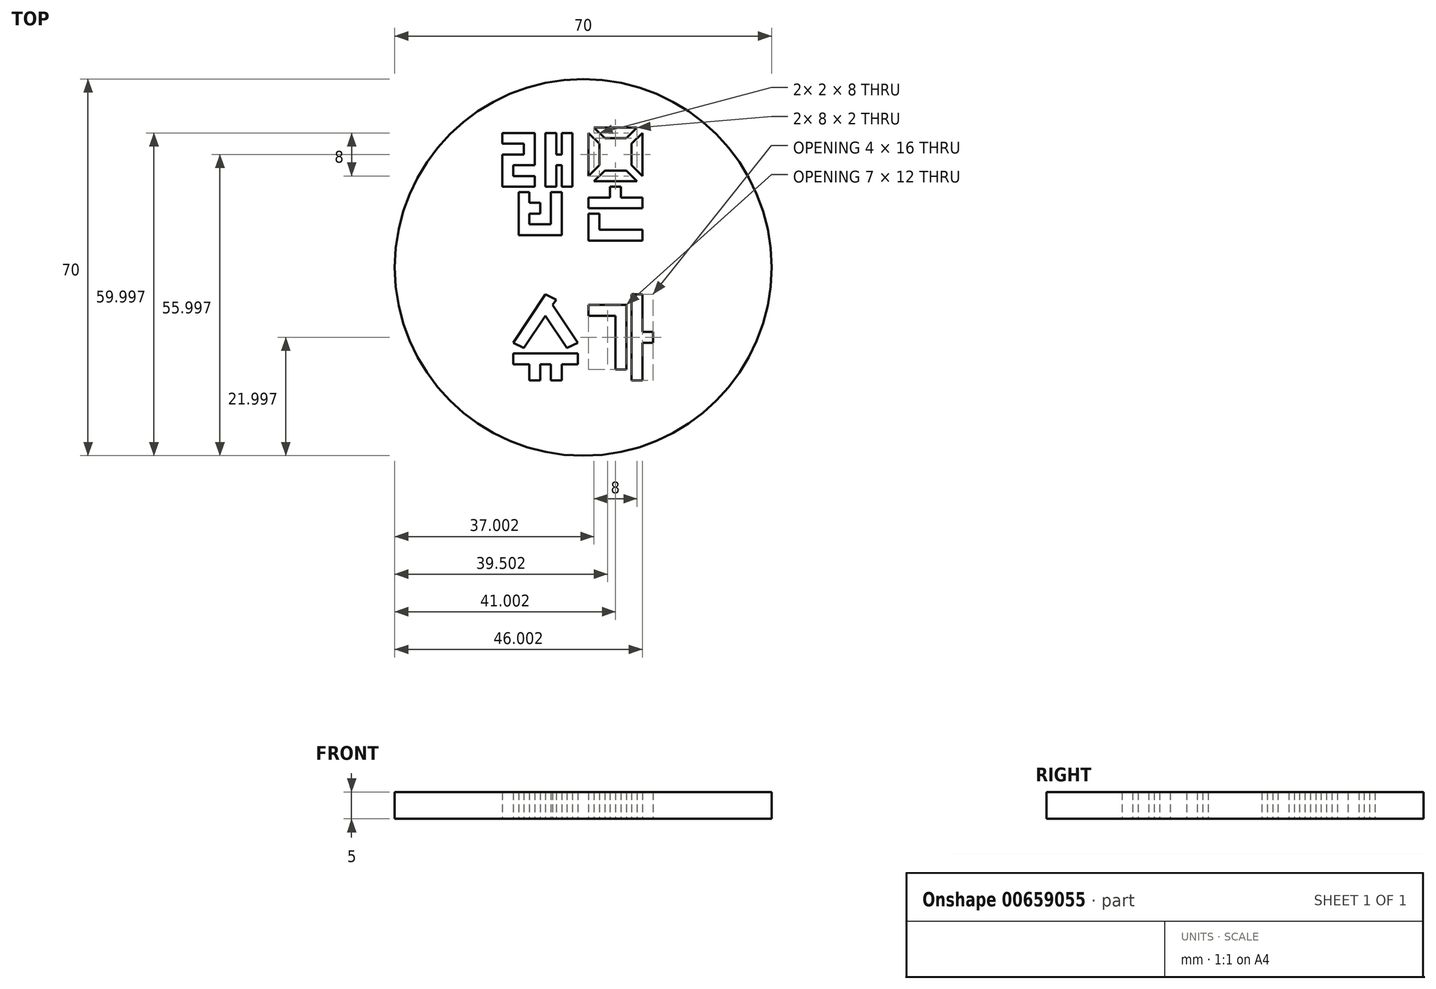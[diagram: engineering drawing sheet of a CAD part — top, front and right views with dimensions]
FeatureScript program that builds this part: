
annotation { "Feature Type Name" : "Feature", "Feature Type Description" : "" }
export const myFeature = defineFeature(function(context is Context, id is Id, definition is map)
    precondition{}
    {
        {
            var Q0;
            Q0=qCreatedBy(makeId("Top.planeOp"),FACE);
            var sketch = newSketch(context, id + "F0", { "sketchPlane" : qUnion([Q0])});
            skLineSegment(sketch, "E0.bottom", {"start": v(-66.05, 21.55) * mm, "end": v(-56.05, 21.55) * mm});
            skLineSegment(sketch, "E0.top", {"start": v(-66.05, 11.55) * mm, "end": v(-60.05, 11.55) * mm});
            skLineSegment(sketch, "E0.left", {"start": v(-66.05, 21.55) * mm, "end": v(-66.05, 19.55) * mm});
            skLineSegment(sketch, "E0.right", {"start": v(-53.05, 21.55) * mm, "end": v(-53.05, 11.55) * mm});
            skLineSegment(sketch, "E1", {"start": v(-66.05, 21.55) * mm, "end": v(-60.05, 21.55) * mm});
            skLineSegment(sketch, "E2", {"start": v(-58.05, 21.55) * mm, "end": v(-58.05, 11.55) * mm});
            skLineSegment(sketch, "E3", {"start": v(-58.05, 11.55) * mm, "end": v(-56.05, 11.55) * mm});
            skLineSegment(sketch, "E4", {"start": v(-56.05, 11.55) * mm, "end": v(-56.05, 15.55) * mm});
            skLineSegment(sketch, "E5", {"start": v(-56.05, 15.55) * mm, "end": v(-55.05, 15.55) * mm});
            skLineSegment(sketch, "E6", {"start": v(-55.05, 15.55) * mm, "end": v(-55.05, 11.55) * mm});
            skLineSegment(sketch, "E7", {"start": v(-56.05, 21.55) * mm, "end": v(-56.05, 17.55) * mm});
            skLineSegment(sketch, "E8", {"start": v(-56.05, 17.55) * mm, "end": v(-55.05, 17.55) * mm});
            skLineSegment(sketch, "E9", {"start": v(-55.05, 17.55) * mm, "end": v(-55.05, 21.55) * mm});
            skLineSegment(sketch, "E10", {"start": v(-60.05, 21.55) * mm, "end": v(-60.05, 15.55) * mm});
            skLineSegment(sketch, "E11", {"start": v(-60.05, 15.55) * mm, "end": v(-64.05, 15.55) * mm});
            skLineSegment(sketch, "E12", {"start": v(-64.05, 15.55) * mm, "end": v(-64.05, 13.55) * mm});
            skLineSegment(sketch, "E13", {"start": v(-64.05, 13.55) * mm, "end": v(-60.05, 13.55) * mm});
            skLineSegment(sketch, "E14", {"start": v(-60.05, 13.55) * mm, "end": v(-60.05, 11.55) * mm});
            skLineSegment(sketch, "E15", {"start": v(-66.05, 19.55) * mm, "end": v(-62.05, 19.55) * mm});
            skLineSegment(sketch, "E16", {"start": v(-62.05, 19.55) * mm, "end": v(-62.05, 17.55) * mm});
            skLineSegment(sketch, "E17", {"start": v(-62.05, 17.55) * mm, "end": v(-66.05, 17.55) * mm});
            skLineSegment(sketch, "E18", {"start": v(-55.05, 10.55) * mm, "end": v(-55.05, 2.55) * mm});
            skLineSegment(sketch, "E19", {"start": v(-55.05, 2.55) * mm, "end": v(-63.05, 2.55) * mm});
            skLineSegment(sketch, "E20", {"start": v(-63.05, 2.55) * mm, "end": v(-63.05, 10.55) * mm});
            skLineSegment(sketch, "E21", {"start": v(-63.05, 10.55) * mm, "end": v(-61.05, 10.55) * mm});
            skLineSegment(sketch, "E22", {"start": v(-61.05, 10.55) * mm, "end": v(-61.05, 8.55) * mm});
            skLineSegment(sketch, "E23", {"start": v(-61.05, 8.55) * mm, "end": v(-59.05, 8.55) * mm});
            skLineSegment(sketch, "E24", {"start": v(-59.05, 8.55) * mm, "end": v(-59.05, 6.55) * mm});
            skLineSegment(sketch, "E25", {"start": v(-59.05, 6.55) * mm, "end": v(-61.05, 6.55) * mm});
            skLineSegment(sketch, "E26", {"start": v(-61.05, 6.55) * mm, "end": v(-61.05, 4.55) * mm});
            skLineSegment(sketch, "E27", {"start": v(-61.05, 4.55) * mm, "end": v(-57.05, 4.55) * mm});
            skLineSegment(sketch, "E28", {"start": v(-57.05, 4.55) * mm, "end": v(-57.05, 10.55) * mm});
            skLineSegment(sketch, "E29", {"start": v(-57.05, 10.55) * mm, "end": v(-55.05, 10.55) * mm});
            skLineSegment(sketch, "E30.trimOffspring", {"start": v(-66.05, 17.55) * mm, "end": v(-66.05, 11.55) * mm});
            skLineSegment(sketch, "E31.trimOffspring", {"start": v(-55.05, 11.55) * mm, "end": v(-53.05, 11.55) * mm});
            skLineSegment(sketch, "E32.trimOffspring", {"start": v(-55.05, 21.55) * mm, "end": v(-53.05, 21.55) * mm});
            skLineSegment(sketch, "E33", {"start": v(-49.05, 22.55) * mm, "end": v(-41.05, 22.55) * mm});
            skLineSegment(sketch, "E34", {"start": v(-41.05, 12.55) * mm, "end": v(-49.05, 12.55) * mm});
            skLineSegment(sketch, "E35.bottom", {"start": v(-47.05, 14.55) * mm, "end": v(-43.05, 14.55) * mm});
            skLineSegment(sketch, "E35.top", {"start": v(-47.05, 20.55) * mm, "end": v(-43.05, 20.55) * mm});
            skLineSegment(sketch, "E35.left", {"start": v(-48.05, 15.55) * mm, "end": v(-48.05, 19.55) * mm});
            skLineSegment(sketch, "E35.right", {"start": v(-42.05, 15.55) * mm, "end": v(-42.05, 19.55) * mm});
            skLineSegment(sketch, "E36", {"start": v(-47.05, 20.55) * mm, "end": v(-49.05, 22.55) * mm});
            skLineSegment(sketch, "E37", {"start": v(-50.05, 21.55) * mm, "end": v(-48.05, 19.55) * mm});
            skLineSegment(sketch, "E38", {"start": v(-42.05, 19.55) * mm, "end": v(-40.05, 21.55) * mm});
            skLineSegment(sketch, "E39", {"start": v(-41.05, 22.55) * mm, "end": v(-43.05, 20.55) * mm});
            skLineSegment(sketch, "E40", {"start": v(-49.05, 12.55) * mm, "end": v(-47.05, 14.55) * mm});
            skLineSegment(sketch, "E41", {"start": v(-50.05, 13.55) * mm, "end": v(-48.05, 15.55) * mm});
            skLineSegment(sketch, "E42", {"start": v(-42.05, 15.55) * mm, "end": v(-40.05, 13.55) * mm});
            skLineSegment(sketch, "E43", {"start": v(-43.05, 14.55) * mm, "end": v(-41.05, 12.55) * mm});
            skLineSegment(sketch, "E44", {"start": v(-40.05, 9.55) * mm, "end": v(-40.05, 7.55) * mm});
            skLineSegment(sketch, "E45", {"start": v(-40.05, 7.55) * mm, "end": v(-50.05, 7.55) * mm});
            skLineSegment(sketch, "E46", {"start": v(-50.05, 7.55) * mm, "end": v(-50.05, 9.55) * mm});
            skLineSegment(sketch, "E47", {"start": v(-50.05, 9.55) * mm, "end": v(-46.05, 9.55) * mm});
            skLineSegment(sketch, "E48", {"start": v(-40.05, 9.55) * mm, "end": v(-44.05, 9.55) * mm});
            skLineSegment(sketch, "E49", {"start": v(-44.05, 9.55) * mm, "end": v(-44.05, 11.55) * mm});
            skLineSegment(sketch, "E50", {"start": v(-44.05, 11.55) * mm, "end": v(-46.05, 11.55) * mm});
            skLineSegment(sketch, "E51", {"start": v(-46.05, 11.55) * mm, "end": v(-46.05, 9.55) * mm});
            skLineSegment(sketch, "E52", {"start": v(-50.05, 6.55) * mm, "end": v(-50.05, 1.55) * mm});
            skLineSegment(sketch, "E53", {"start": v(-50.05, 1.55) * mm, "end": v(-40.05, 1.55) * mm});
            skLineSegment(sketch, "E54", {"start": v(-40.05, 1.55) * mm, "end": v(-40.05, 3.55) * mm});
            skLineSegment(sketch, "E55", {"start": v(-40.05, 3.55) * mm, "end": v(-48.05, 3.55) * mm});
            skLineSegment(sketch, "E56", {"start": v(-48.05, 3.55) * mm, "end": v(-48.05, 6.55) * mm});
            skLineSegment(sketch, "E57", {"start": v(-48.05, 6.55) * mm, "end": v(-50.05, 6.55) * mm});
            skLineSegment(sketch, "E58.trimOffspring", {"start": v(-50.05, 13.55) * mm, "end": v(-50.05, 21.55) * mm});
            skPoint(sketch, "E59.end.orphan", {"position": v(-48.05, 12.55) * mm});
            skPoint(sketch, "E60.end.orphan", {"position": v(-50.05, 14.55) * mm});
            skLineSegment(sketch, "E61", {"start": v(-40.05, 21.55) * mm, "end": v(-40.05, 13.55) * mm});
            skLineSegment(sketch, "E62.trimOffspring", {"start": v(-44.05, 9.55) * mm, "end": v(-40.05, 9.55) * mm});
            skLineSegment(sketch, "E63", {"start": v(-40.05, -8.45) * mm, "end": v(-40.05, -15.45) * mm});
            skLineSegment(sketch, "E64", {"start": v(-40.05, -24.45) * mm, "end": v(-42.05, -24.45) * mm});
            skLineSegment(sketch, "E65", {"start": v(-42.05, -24.45) * mm, "end": v(-42.05, -22.45) * mm});
            skLineSegment(sketch, "E66", {"start": v(-43.05, -22.45) * mm, "end": v(-45.05, -22.45) * mm});
            skLineSegment(sketch, "E67", {"start": v(-45.05, -22.45) * mm, "end": v(-45.05, -12.45) * mm});
            skLineSegment(sketch, "E68", {"start": v(-45.05, -12.45) * mm, "end": v(-50.05, -12.45) * mm});
            skLineSegment(sketch, "E69", {"start": v(-50.05, -12.45) * mm, "end": v(-50.05, -10.45) * mm});
            skLineSegment(sketch, "E70", {"start": v(-50.05, -10.45) * mm, "end": v(-43.05, -10.45) * mm});
            skLineSegment(sketch, "E71", {"start": v(-43.05, -10.45) * mm, "end": v(-43.05, -22.45) * mm});
            skLineSegment(sketch, "E72", {"start": v(-42.05, -22.45) * mm, "end": v(-42.05, -8.45) * mm});
            skLineSegment(sketch, "E73", {"start": v(-42.05, -8.45) * mm, "end": v(-40.05, -8.45) * mm});
            skLineSegment(sketch, "E74", {"start": v(-40.05, -24.45) * mm, "end": v(-40.05, -17.45) * mm});
            skLineSegment(sketch, "E75", {"start": v(-40.05, -17.45) * mm, "end": v(-38.05, -17.45) * mm});
            skLineSegment(sketch, "E76", {"start": v(-38.05, -17.45) * mm, "end": v(-38.05, -15.45) * mm});
            skLineSegment(sketch, "E77", {"start": v(-38.05, -15.45) * mm, "end": v(-40.05, -15.45) * mm});
            skLineSegment(sketch, "E78.trimOffspring", {"start": v(-40.05, -17.45) * mm, "end": v(-40.05, -24.45) * mm});
            skLineSegment(sketch, "E79", {"start": v(-61.05, -24.45) * mm, "end": v(-59.05, -24.45) * mm});
            skLineSegment(sketch, "E80", {"start": v(-57.05, -24.45) * mm, "end": v(-55.05, -24.45) * mm});
            skLineSegment(sketch, "E81", {"start": v(-64.05, -19.45) * mm, "end": v(-64.05, -21.45) * mm});
            skLineSegment(sketch, "E82", {"start": v(-64.05, -21.45) * mm, "end": v(-61.05, -21.45) * mm});
            skLineSegment(sketch, "E83", {"start": v(-61.05, -21.45) * mm, "end": v(-61.05, -24.45) * mm});
            skLineSegment(sketch, "E84", {"start": v(-59.05, -24.45) * mm, "end": v(-59.05, -21.45) * mm});
            skLineSegment(sketch, "E85", {"start": v(-59.05, -21.45) * mm, "end": v(-57.05, -21.45) * mm});
            skLineSegment(sketch, "E86", {"start": v(-57.05, -21.45) * mm, "end": v(-57.05, -24.45) * mm});
            skLineSegment(sketch, "E87", {"start": v(-55.05, -24.45) * mm, "end": v(-55.05, -21.45) * mm});
            skLineSegment(sketch, "E88", {"start": v(-55.05, -21.45) * mm, "end": v(-52.05, -21.45) * mm});
            skLineSegment(sketch, "E89", {"start": v(-52.05, -21.45) * mm, "end": v(-52.05, -19.45) * mm});
            skLineSegment(sketch, "E90", {"start": v(-52.05, -19.45) * mm, "end": v(-64.05, -19.45) * mm});
            skLineSegment(sketch, "E91.trimOffspring", {"start": v(-55.05, -24.45) * mm, "end": v(-57.05, -24.45) * mm});
            skLineSegment(sketch, "E92.trimOffspring", {"start": v(-59.05, -24.45) * mm, "end": v(-61.05, -24.45) * mm});
            skLineSegment(sketch, "E93", {"start": v(-58.05, -8.45) * mm, "end": v(-64.05, -17.45) * mm});
            skLineSegment(sketch, "E94", {"start": v(-56.05, -9.45) * mm, "end": v(-56.71, -10.45) * mm});
            skLineSegment(sketch, "E95", {"start": v(-58.05, -8.45) * mm, "end": v(-56.05, -9.45) * mm});
            skLineSegment(sketch, "E96", {"start": v(-64.05, -17.45) * mm, "end": v(-62.05, -18.45) * mm});
            skLineSegment(sketch, "E97", {"start": v(-52.05, -17.45) * mm, "end": v(-54.05, -18.45) * mm});
            skLineSegment(sketch, "E98", {"start": v(-54.05, -18.45) * mm, "end": v(-58.05, -12.45) * mm});
            skLineSegment(sketch, "E99", {"start": v(-52.05, -17.45) * mm, "end": v(-56.71, -10.45) * mm});
            skLineSegment(sketch, "E100.trimOffspring", {"start": v(-58.05, -12.45) * mm, "end": v(-62.05, -18.45) * mm});
            skCircle(sketch, "E101", {"center": v(-51.05, -3.45) * mm, "radius": 35 * mm});
            skSolve(sketch);
        }
        {
            var Q0;
            Q0=makeQuery(id+"F0.imprint","IMPRINT",FACE,{"disambiguationData":[TD([[makeQuery(id+"F0.imprint","IMPRINT",EDGE,{"derivedFrom":sQuery(id+"F0.wireOp",EDGE,"E0.top")}),-1.0]])]});
            extrude(context, id + "F1", {"entities" : qUnion([Q0]), "depth" : 5 * mm, "offsetDistance" : 25 * mm});
        }
    });
